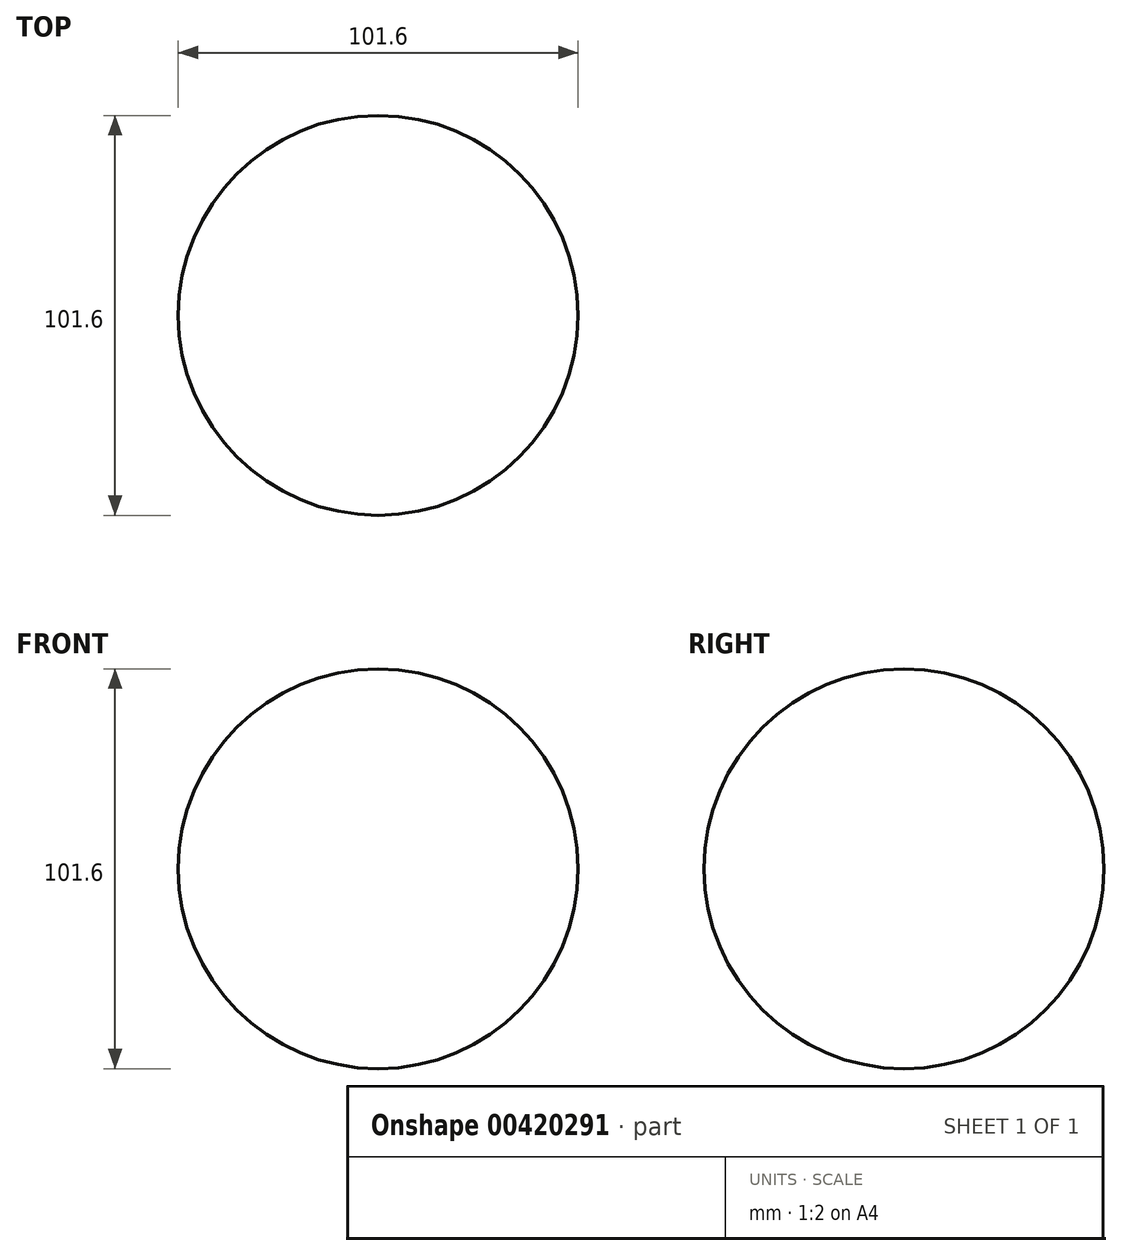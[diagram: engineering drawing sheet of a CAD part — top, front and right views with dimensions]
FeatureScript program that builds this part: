
annotation { "Feature Type Name" : "Feature", "Feature Type Description" : "" }
export const myFeature = defineFeature(function(context is Context, id is Id, definition is map)
    precondition{}
    {
        {
            var Q0;
            Q0=qCreatedBy(makeId("Front.planeOp"),FACE);
            var sketch = newSketch(context, id + "F0", { "sketchPlane" : qUnion([Q0])});
            skArc(sketch, "E0", {"start": v(0, 50.8) * mm, "mid": v(50.8, 0) * mm, "end": v(0, -50.8) * mm});
            skLineSegment(sketch, "E1", {"start": v(0, 50.8) * mm, "end": v(0, -50.8) * mm});
            skSolve(sketch);
        }
        {
            var Q0;
            Q0 = qSketchRegion(id + "F0", true);
            var Q1;
            Q1=sQuery(id+"F0.wireOp",EDGE,"E1");
            revolve(context, id + "F1", {"entities" : qUnion([Q0]), "axis" : qUnion([Q1]), "revolveType" : RevolveType.FULL});
        }
    });
